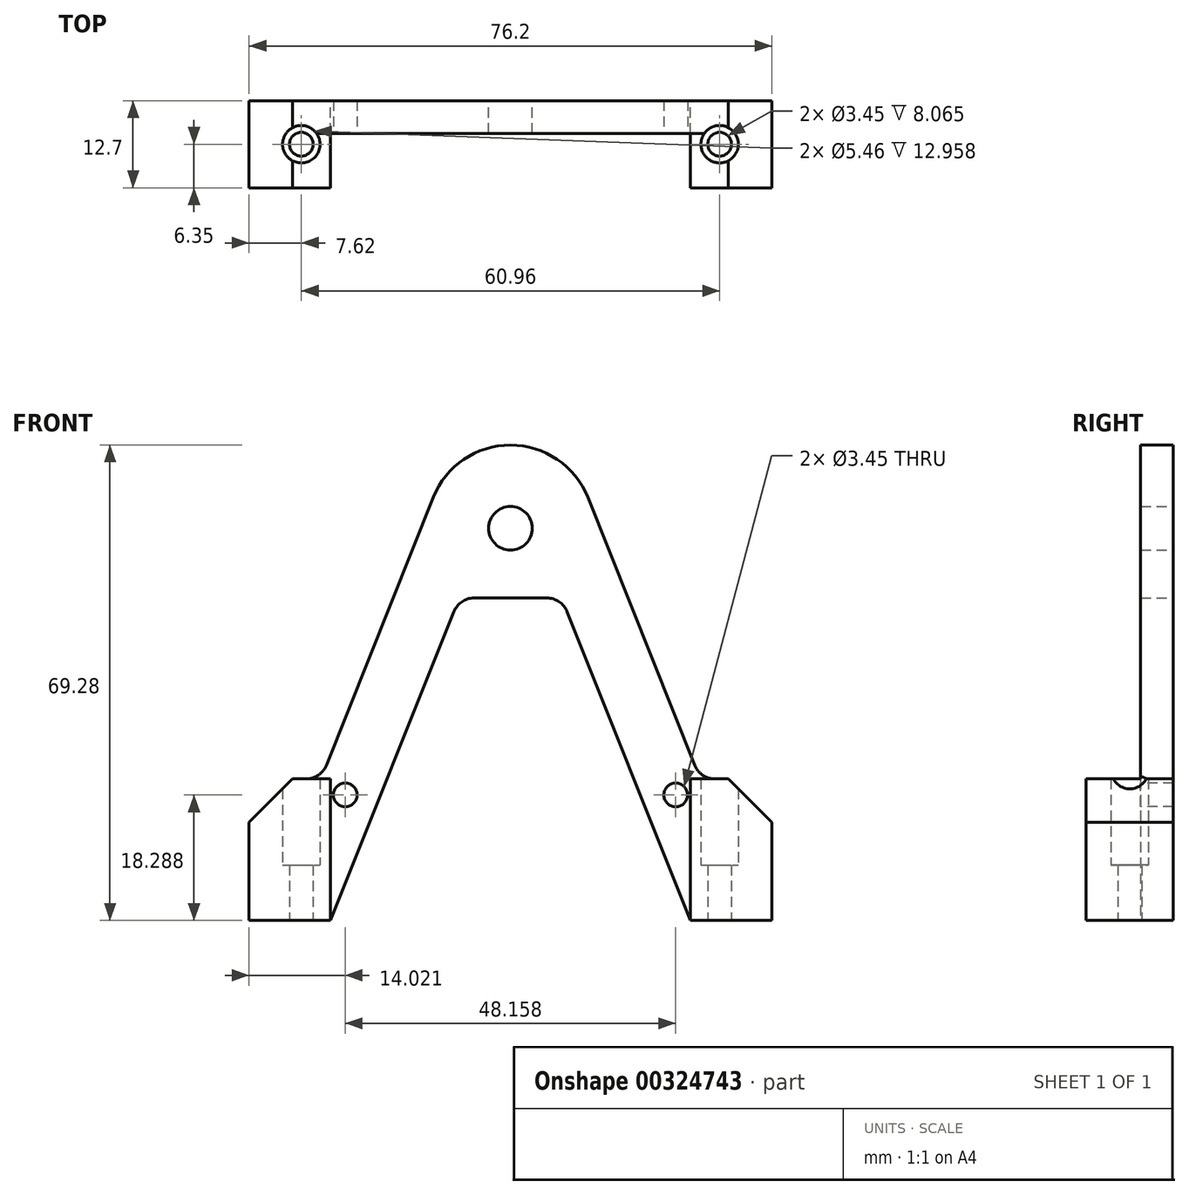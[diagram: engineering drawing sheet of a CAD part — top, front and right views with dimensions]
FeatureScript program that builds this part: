
annotation { "Feature Type Name" : "Feature", "Feature Type Description" : "" }
export const myFeature = defineFeature(function(context is Context, id is Id, definition is map)
    precondition{}
    {
        {
            var Q0;
            Q0=qCreatedBy(makeId("Front.planeOp"),FACE);
            var sketch = newSketch(context, id + "F0", { "sketchPlane" : qUnion([Q0])});
            skLineSegment(sketch, "E0", {"start": v(-38.1, 0) * mm, "end": v(-38.1, 59.47) * mm, "construction": true});
            skLineSegment(sketch, "E1.MirrorCS", {"start": v(38.1, 0) * mm, "end": v(38.1, 59.47) * mm, "construction": true});
            skLineSegment(sketch, "E2", {"start": v(-48.16, 57.15) * mm, "end": v(47.02, 57.15) * mm, "construction": true});
            skCircle(sketch, "E3", {"center": v(0, 57.15) * mm, "radius": 3.18 * mm});
            skLineSegment(sketch, "E4", {"start": v(-43.35, 43.82) * mm, "end": v(48.99, 43.82) * mm, "construction": true});
            skLineSegment(sketch, "E5", {"start": v(-5.3, 0) * mm, "end": v(-5.3, 68.46) * mm, "construction": true});
            skLineSegment(sketch, "E6.MirrorCS", {"start": v(5.3, 0) * mm, "end": v(5.3, 68.46) * mm, "construction": true});
            skArc(sketch, "E7", {"start": v(-5.3, 47) * mm, "mid": v(-7.09, 46.44) * mm, "end": v(-8.26, 45) * mm});
            skArc(sketch, "E8", {"start": v(8.26, 45) * mm, "mid": v(7.09, 46.44) * mm, "end": v(5.3, 47) * mm});
            skLineSegment(sketch, "E9", {"start": v(-26.21, -2.18) * mm, "end": v(-26.21, 12.81) * mm, "construction": true});
            skLineSegment(sketch, "E10.MirrorCS", {"start": v(26.21, -2.18) * mm, "end": v(26.21, 12.81) * mm, "construction": true});
            skLineSegment(sketch, "E11", {"start": v(-26.21, 0) * mm, "end": v(-8.26, 45) * mm});
            skLineSegment(sketch, "E12", {"start": v(-5.3, 47) * mm, "end": v(5.3, 47) * mm});
            skLineSegment(sketch, "E13.MirrorCS", {"start": v(26.21, 0) * mm, "end": v(8.26, 45) * mm});
            skLineSegment(sketch, "E14", {"start": v(-41.13, 20.62) * mm, "end": v(27.7, 20.62) * mm, "construction": true});
            skPoint(sketch, "E15.orphan", {"position": v(-5.65, 72.14) * mm});
            skPoint(sketch, "E16.orphan", {"position": v(5.65, 72.14) * mm});
            skLineSegment(sketch, "E17", {"start": v(-26.21, 20.62) * mm, "end": v(-38.1, 20.62) * mm});
            skLineSegment(sketch, "E18", {"start": v(-38.1, 20.62) * mm, "end": v(-38.1, 0) * mm});
            skLineSegment(sketch, "E19", {"start": v(26.21, 20.62) * mm, "end": v(38.1, 20.62) * mm});
            skLineSegment(sketch, "E20", {"start": v(26.21, 0) * mm, "end": v(38.1, 0) * mm});
            skLineSegment(sketch, "E21", {"start": v(38.1, 20.62) * mm, "end": v(38.1, 0) * mm});
            skLineSegment(sketch, "E22", {"start": v(-38.1, 0) * mm, "end": v(-26.21, 0) * mm});
            skLineSegment(sketch, "E23.0", {"start": v(27.64, 20.62) * mm, "end": v(11.27, 61.65) * mm});
            skLineSegment(sketch, "E24.MirrorCS", {"start": v(-27.64, 20.62) * mm, "end": v(-11.27, 61.65) * mm});
            skArc(sketch, "E25", {"start": v(-11.27, 61.65) * mm, "mid": v(0, 69.28) * mm, "end": v(11.27, 61.65) * mm});
            skSolve(sketch);
        }
        {
            var Q0;
            Q0=makeQuery(id+"F0.imprint","IMPRINT",FACE,{"disambiguationData":[TD([[makeQuery(id+"F0.imprint","IMPRINT",EDGE,{"derivedFrom":sQuery(id+"F0.wireOp",EDGE,"E3")}),-1.0]])]});
            extrude(context, id + "F1", {"entities" : qUnion([Q0]), "depth" : 4.78 * mm, "offsetDistance" : 25.4 * mm});
        }
        {
            var Q0;
            Q0=makeQuery(id+"F1.opExtrude","CAP_FACE",FACE,{"disambiguationData":[OSD([sQuery(id+"F0.wireOp",EDGE,"E3"),sQuery(id+"F0.wireOp",EDGE,"E7"),sQuery(id+"F0.wireOp",EDGE,"E8"),sQuery(id+"F0.wireOp",EDGE,"E11"),sQuery(id+"F0.wireOp",EDGE,"E12"),sQuery(id+"F0.wireOp",EDGE,"E13.MirrorCS"),sQuery(id+"F0.wireOp",EDGE,"E17"),sQuery(id+"F0.wireOp",EDGE,"E18"),sQuery(id+"F0.wireOp",EDGE,"E19"),sQuery(id+"F0.wireOp",EDGE,"E20"),sQuery(id+"F0.wireOp",EDGE,"E21"),sQuery(id+"F0.wireOp",EDGE,"E22"),sQuery(id+"F0.wireOp",EDGE,"E23.0"),sQuery(id+"F0.wireOp",EDGE,"E24.MirrorCS"),sQuery(id+"F0.wireOp",EDGE,"E25")])],"isStart":false});
            var sketch = newSketch(context, id + "F2", { "sketchPlane" : qUnion([Q0])});
            skLineSegment(sketch, "E26.bottom", {"start": v(-38.1, 20.62) * mm, "end": v(-26.21, 20.62) * mm});
            skLineSegment(sketch, "E26.top", {"start": v(-38.1, 0) * mm, "end": v(-26.21, 0) * mm});
            skLineSegment(sketch, "E26.left", {"start": v(-38.1, 20.62) * mm, "end": v(-38.1, 0) * mm});
            skLineSegment(sketch, "E26.right", {"start": v(-26.21, 20.62) * mm, "end": v(-26.21, 0) * mm});
            skLineSegment(sketch, "E27.bottom", {"start": v(38.1, 20.62) * mm, "end": v(26.21, 20.62) * mm});
            skLineSegment(sketch, "E27.top", {"start": v(38.1, 0) * mm, "end": v(26.21, 0) * mm});
            skLineSegment(sketch, "E27.left", {"start": v(38.1, 20.62) * mm, "end": v(38.1, 0) * mm});
            skLineSegment(sketch, "E27.right", {"start": v(26.21, 20.62) * mm, "end": v(26.21, 0) * mm});
            skSolve(sketch);
        }
        {
            var Q0;
            Q0=makeQuery(id+"F2.imprint","IMPRINT",FACE,{"disambiguationData":[TD([[makeQuery(id+"F2.imprint","IMPRINT",EDGE,{"derivedFrom":sQuery(id+"F2.wireOp",EDGE,"E26.top")}),1.0]])]});
            var Q1;
            Q1=makeQuery(id+"F2.imprint","IMPRINT",FACE,{"disambiguationData":[TD([[makeQuery(id+"F2.imprint","IMPRINT",EDGE,{"derivedFrom":sQuery(id+"F2.wireOp",EDGE,"E27.top")}),1.0]])]});
            extrude(context, id + "F3", {"entities" : qUnion([Q0, Q1]), "operationType" : NewBodyOperationType.ADD, "depth" : 7.92 * mm, "offsetDistance" : 25.4 * mm});
        }
        {
            var Q0;
            Q0=makeQuery(id+"F3.boolean.opBoolean","MERGE",EDGE,{"derivedFrom":[makeQuery(id+"F1.opExtrude","SWEPT_EDGE",EDGE,{"disambiguationData":[OSD([sQuery(id+"F0.wireOp",EDGE,"E19"),sQuery(id+"F0.wireOp",EDGE,"E21")])]}),makeQuery(id+"F3.opExtrude","SWEPT_EDGE",EDGE,{"disambiguationData":[OSD([sQuery(id+"F2.wireOp",EDGE,"E27.bottom"),sQuery(id+"F2.wireOp",EDGE,"E27.left")])]})]});
            var Q1;
            Q1=makeQuery(id+"F3.boolean.opBoolean","MERGE",EDGE,{"derivedFrom":[makeQuery(id+"F1.opExtrude","SWEPT_EDGE",EDGE,{"disambiguationData":[OSD([sQuery(id+"F0.wireOp",EDGE,"E17"),sQuery(id+"F0.wireOp",EDGE,"E18")])]}),makeQuery(id+"F3.opExtrude","SWEPT_EDGE",EDGE,{"disambiguationData":[OSD([sQuery(id+"F2.wireOp",EDGE,"E26.bottom"),sQuery(id+"F2.wireOp",EDGE,"E26.left")])]})]});
            chamfer(context, id + "F4", {"entities" : qUnion([Q0, Q1]), "width" : 6.35 * mm, "tangentPropagation" : true});
        }
        {
            var Q0;
            Q0=makeQuery(id+"F3.boolean.opBoolean","MERGE",FACE,{"derivedFrom":[makeQuery(id+"F1.opExtrude","SWEPT_FACE",FACE,{"disambiguationData":[OSD([sQuery(id+"F0.wireOp",EDGE,"E17")])]}),makeQuery(id+"F3.opExtrude","SWEPT_FACE",FACE,{"disambiguationData":[OSD([sQuery(id+"F2.wireOp",EDGE,"E26.bottom")])]})]});
            var sketch = newSketch(context, id + "F5", { "sketchPlane" : qUnion([Q0])});
            skPoint(sketch, "E28", {"position": v(-30.48, -6.35) * mm});
            skPoint(sketch, "E29", {"position": v(40.23, -6.35) * mm});
            skPoint(sketch, "E30", {"position": v(30.48, -6.35) * mm});
            skSolve(sketch);
        }
        {
            var Q0;
            Q0=sQuery(id+"F5.wireOp",VERTEX,"E28");
            var Q1;
            Q1=sQuery(id+"F5.wireOp",VERTEX,"E30");
            var Q2;
            Q2=makeQuery(id+"F1.opExtrude","SWEPT_BODY",BODY,{"disambiguationData":[OSD([sQuery(id+"F0.wireOp",EDGE,"E3"),sQuery(id+"F0.wireOp",EDGE,"E7"),sQuery(id+"F0.wireOp",EDGE,"E8"),sQuery(id+"F0.wireOp",EDGE,"E11"),sQuery(id+"F0.wireOp",EDGE,"E12"),sQuery(id+"F0.wireOp",EDGE,"E13.MirrorCS"),sQuery(id+"F0.wireOp",EDGE,"E17"),sQuery(id+"F0.wireOp",EDGE,"E18"),sQuery(id+"F0.wireOp",EDGE,"E19"),sQuery(id+"F0.wireOp",EDGE,"E20"),sQuery(id+"F0.wireOp",EDGE,"E21"),sQuery(id+"F0.wireOp",EDGE,"E22"),sQuery(id+"F0.wireOp",EDGE,"E23.0"),sQuery(id+"F0.wireOp",EDGE,"E24.MirrorCS"),sQuery(id+"F0.wireOp",EDGE,"E25")])]});
            hole(context, id + "F6", {"style" : HoleStyle.C_BORE, "endStyle" : HoleEndStyle.THROUGH, "holeDiameter" : 3.45 * mm, "cBoreDiameter" : 5.46 * mm, "cBoreDepth" : 11.1 * mm, "majorDiameter" : 6.35 * mm, "tappedDepth" : 12.7 * mm, "tapClearance" : 3, "locations" : qUnion([Q0, Q1]), "scope" : qUnion([Q2])});
        }
        {
            var Q0;
            Q0=makeQuery(id+"F1.opExtrude","CAP_FACE",FACE,{"disambiguationData":[OSD([sQuery(id+"F0.wireOp",EDGE,"E3"),sQuery(id+"F0.wireOp",EDGE,"E7"),sQuery(id+"F0.wireOp",EDGE,"E8"),sQuery(id+"F0.wireOp",EDGE,"E11"),sQuery(id+"F0.wireOp",EDGE,"E12"),sQuery(id+"F0.wireOp",EDGE,"E13.MirrorCS"),sQuery(id+"F0.wireOp",EDGE,"E17"),sQuery(id+"F0.wireOp",EDGE,"E18"),sQuery(id+"F0.wireOp",EDGE,"E19"),sQuery(id+"F0.wireOp",EDGE,"E20"),sQuery(id+"F0.wireOp",EDGE,"E21"),sQuery(id+"F0.wireOp",EDGE,"E22"),sQuery(id+"F0.wireOp",EDGE,"E23.0"),sQuery(id+"F0.wireOp",EDGE,"E24.MirrorCS"),sQuery(id+"F0.wireOp",EDGE,"E25")])],"isStart":true});
            var sketch = newSketch(context, id + "F7", { "sketchPlane" : qUnion([Q0])});
            skPoint(sketch, "E31", {"position": v(-24.08, 18.29) * mm});
            skPoint(sketch, "E32", {"position": v(24.08, 18.29) * mm});
            skSolve(sketch);
        }
        {
            var Q0;
            Q0=sQuery(id+"F7.wireOp",VERTEX,"E31");
            var Q1;
            Q1=sQuery(id+"F7.wireOp",VERTEX,"E32");
            var Q2;
            Q2=makeQuery(id+"F1.opExtrude","SWEPT_BODY",BODY,{"disambiguationData":[OSD([sQuery(id+"F0.wireOp",EDGE,"E3"),sQuery(id+"F0.wireOp",EDGE,"E7"),sQuery(id+"F0.wireOp",EDGE,"E8"),sQuery(id+"F0.wireOp",EDGE,"E11"),sQuery(id+"F0.wireOp",EDGE,"E12"),sQuery(id+"F0.wireOp",EDGE,"E13.MirrorCS"),sQuery(id+"F0.wireOp",EDGE,"E17"),sQuery(id+"F0.wireOp",EDGE,"E18"),sQuery(id+"F0.wireOp",EDGE,"E19"),sQuery(id+"F0.wireOp",EDGE,"E20"),sQuery(id+"F0.wireOp",EDGE,"E21"),sQuery(id+"F0.wireOp",EDGE,"E22"),sQuery(id+"F0.wireOp",EDGE,"E23.0"),sQuery(id+"F0.wireOp",EDGE,"E24.MirrorCS"),sQuery(id+"F0.wireOp",EDGE,"E25")])]});
            hole(context, id + "F8", {"style" : HoleStyle.SIMPLE, "endStyle" : HoleEndStyle.BLIND, "holeDiameter" : 3.45 * mm, "majorDiameter" : 6.35 * mm, "holeDepth" : 5.08 * mm, "tappedDepth" : 12.7 * mm, "tapClearance" : 3, "locations" : qUnion([Q0, Q1]), "scope" : qUnion([Q2])});
        }
        {
            var Q0;
            Q0=makeQuery(id+"F1.opExtrude","SWEPT_EDGE",EDGE,{"disambiguationData":[OSD([sQuery(id+"F0.wireOp",EDGE,"E17"),sQuery(id+"F0.wireOp",EDGE,"E24.MirrorCS")])]});
            var Q1;
            Q1=makeQuery(id+"F1.opExtrude","SWEPT_EDGE",EDGE,{"disambiguationData":[OSD([sQuery(id+"F0.wireOp",EDGE,"E19"),sQuery(id+"F0.wireOp",EDGE,"E23.0")])]});
            fillet(context, id + "F9", {"entities" : qUnion([Q0, Q1]), "tangentPropagation" : true, "radius" : 3.17 * mm, "defaultsChanged" : true, "vertexSettings" : [], "allowEdgeOverflow" : false});
        }
    });
